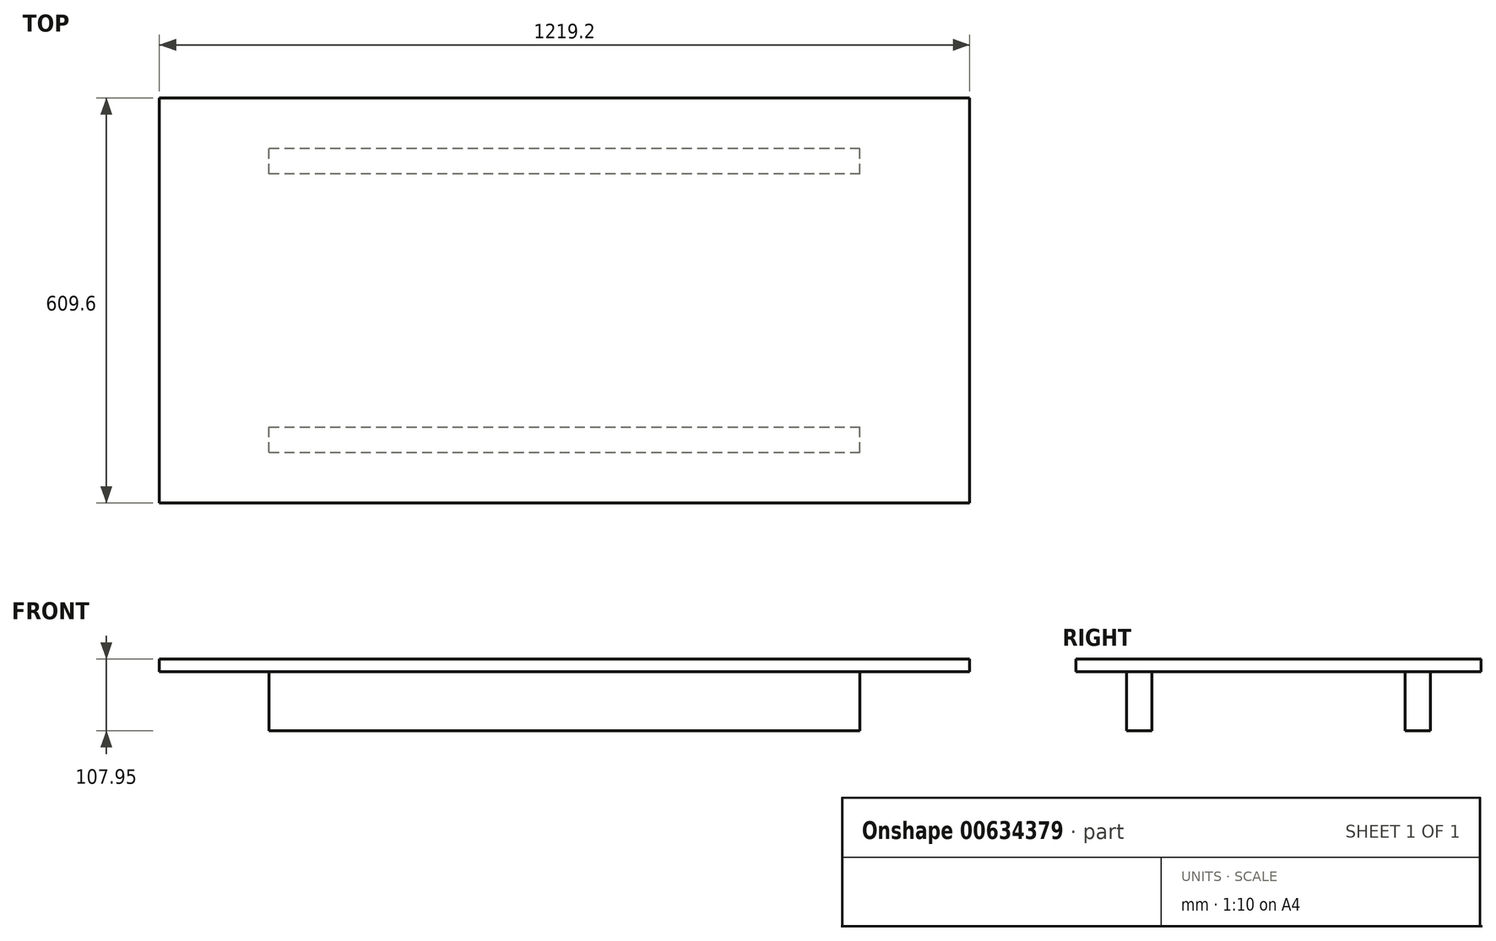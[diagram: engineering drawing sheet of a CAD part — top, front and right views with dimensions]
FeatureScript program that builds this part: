
annotation { "Feature Type Name" : "Feature", "Feature Type Description" : "" }
export const myFeature = defineFeature(function(context is Context, id is Id, definition is map)
    precondition{}
    {
        {
            var Q0;
            Q0=qCreatedBy(makeId("Top.planeOp"),FACE);
            var sketch = newSketch(context, id + "F0", { "sketchPlane" : qUnion([Q0])});
            skLineSegment(sketch, "E0.bottom", {"start": v(-609.6, 304.8) * mm, "end": v(609.6, 304.8) * mm});
            skLineSegment(sketch, "E0.top", {"start": v(-609.6, -304.8) * mm, "end": v(609.6, -304.8) * mm});
            skLineSegment(sketch, "E0.left", {"start": v(-609.6, 304.8) * mm, "end": v(-609.6, -304.8) * mm});
            skLineSegment(sketch, "E0.right", {"start": v(609.6, 304.8) * mm, "end": v(609.6, -304.8) * mm});
            skSolve(sketch);
        }
        {
            var Q0;
            Q0 = qSketchRegion(id + "F0", true);
            extrude(context, id + "F1", {"entities" : qUnion([Q0]), "depth" : 19.05 * mm, "offsetDistance" : 25.4 * mm});
        }
        {
            var Q0;
            Q0=makeQuery(id+"F1.opExtrude","CAP_FACE",FACE,{"disambiguationData":[OSD([sQuery(id+"F0.wireOp",EDGE,"E0.bottom"),sQuery(id+"F0.wireOp",EDGE,"E0.top"),sQuery(id+"F0.wireOp",EDGE,"E0.left"),sQuery(id+"F0.wireOp",EDGE,"E0.right")])],"isStart":true});
            var sketch = newSketch(context, id + "F2", { "sketchPlane" : qUnion([Q0])});
            skLineSegment(sketch, "E1.bottom", {"start": v(444.5, 228.6) * mm, "end": v(533.4, 228.6) * mm});
            skLineSegment(sketch, "E1.top", {"start": v(444.5, 190.5) * mm, "end": v(533.4, 190.5) * mm});
            skLineSegment(sketch, "E1.left", {"start": v(444.5, 228.6) * mm, "end": v(444.5, 190.5) * mm});
            skLineSegment(sketch, "E1.right", {"start": v(533.4, 228.6) * mm, "end": v(533.4, 190.5) * mm});
            skLineSegment(sketch, "E2.bottom", {"start": v(-533.4, 228.6) * mm, "end": v(-444.5, 228.6) * mm});
            skLineSegment(sketch, "E2.top", {"start": v(-533.4, 190.5) * mm, "end": v(-444.5, 190.5) * mm});
            skLineSegment(sketch, "E2.left", {"start": v(-533.4, 228.6) * mm, "end": v(-533.4, 190.5) * mm});
            skLineSegment(sketch, "E2.right", {"start": v(-444.5, 228.6) * mm, "end": v(-444.5, 190.5) * mm});
            skLineSegment(sketch, "E3.bottom", {"start": v(-533.4, -190.5) * mm, "end": v(-444.5, -190.5) * mm});
            skLineSegment(sketch, "E3.top", {"start": v(-533.4, -228.6) * mm, "end": v(-444.5, -228.6) * mm});
            skLineSegment(sketch, "E3.left", {"start": v(-533.4, -190.5) * mm, "end": v(-533.4, -228.6) * mm});
            skLineSegment(sketch, "E3.right", {"start": v(-444.5, -190.5) * mm, "end": v(-444.5, -228.6) * mm});
            skLineSegment(sketch, "E4.bottom", {"start": v(444.5, -190.5) * mm, "end": v(533.4, -190.5) * mm});
            skLineSegment(sketch, "E4.top", {"start": v(444.5, -228.6) * mm, "end": v(533.4, -228.6) * mm});
            skLineSegment(sketch, "E4.left", {"start": v(444.5, -190.5) * mm, "end": v(444.5, -228.6) * mm});
            skLineSegment(sketch, "E4.right", {"start": v(533.4, -190.5) * mm, "end": v(533.4, -228.6) * mm});
            skLineSegment(sketch, "E5.bottom", {"start": v(-444.5, 228.6) * mm, "end": v(444.5, 228.6) * mm});
            skLineSegment(sketch, "E5.top", {"start": v(-444.5, 190.5) * mm, "end": v(444.5, 190.5) * mm});
            skLineSegment(sketch, "E6.bottom", {"start": v(533.4, 190.5) * mm, "end": v(488.95, 190.5) * mm});
            skLineSegment(sketch, "E6.top", {"start": v(533.4, -190.5) * mm, "end": v(488.95, -190.5) * mm});
            skLineSegment(sketch, "E7.bottom", {"start": v(444.5, -228.6) * mm, "end": v(-444.5, -228.6) * mm});
            skLineSegment(sketch, "E7.top", {"start": v(444.5, -190.5) * mm, "end": v(-444.5, -190.5) * mm});
            skLineSegment(sketch, "E7.left", {"start": v(444.5, -228.6) * mm, "end": v(444.5, -190.5) * mm});
            skLineSegment(sketch, "E7.right", {"start": v(-444.5, -228.6) * mm, "end": v(-444.5, -190.5) * mm});
            skLineSegment(sketch, "E8.bottom", {"start": v(-533.4, 190.5) * mm, "end": v(-495.3, 190.5) * mm});
            skLineSegment(sketch, "E8.top", {"start": v(-533.4, -190.5) * mm, "end": v(-495.3, -190.5) * mm});
            skLineSegment(sketch, "E8.left", {"start": v(-533.4, 190.5) * mm, "end": v(-533.4, -190.5) * mm});
            skLineSegment(sketch, "E8.right", {"start": v(-495.3, 190.5) * mm, "end": v(-495.3, -190.5) * mm});
            skLineSegment(sketch, "E9.bottom", {"start": v(533.4, 190.5) * mm, "end": v(495.3, 190.5) * mm});
            skLineSegment(sketch, "E9.top", {"start": v(533.4, -190.5) * mm, "end": v(495.3, -190.5) * mm});
            skLineSegment(sketch, "E9.left", {"start": v(533.4, 190.5) * mm, "end": v(533.4, -190.5) * mm});
            skLineSegment(sketch, "E9.right", {"start": v(495.3, 190.5) * mm, "end": v(495.3, -190.5) * mm});
            skSolve(sketch);
        }
        {
            var Q0;
            Q0=makeQuery(id+"F2.imprint","IMPRINT",FACE,{"disambiguationData":[TD([[makeQuery(id+"F2.imprint","IMPRINT",EDGE,{"derivedFrom":sQuery(id+"F2.wireOp",EDGE,"E5.bottom")}),-1.0]])]});
            var Q1;
            Q1=makeQuery(id+"F2.imprint","IMPRINT",FACE,{"disambiguationData":[TD([[makeQuery(id+"F2.imprint","IMPRINT",EDGE,{"derivedFrom":sQuery(id+"F2.wireOp",EDGE,"E7.bottom")}),-1.0]])]});
            var Q2;
            Q2=makeQuery(id+"F2.imprint","IMPRINT",FACE,{"disambiguationData":[TD([[makeQuery(id+"F2.imprint","IMPRINT",EDGE,{"derivedFrom":sQuery(id+"F2.wireOp",EDGE,"E8.bottom")}),-1.0]])]});
            var Q3;
            Q3=makeQuery(id+"F2.imprint","IMPRINT",FACE,{"disambiguationData":[TD([[makeQuery(id+"F2.imprint","IMPRINT",EDGE,{"derivedFrom":sQuery(id+"F2.wireOp",EDGE,"E9.bottom")}),1.0]])]});
            extrude(context, id + "F3", {"entities" : qUnion([Q0, Q1, Q2, Q3]), "operationType" : NewBodyOperationType.ADD, "depth" : 88.9 * mm, "offsetDistance" : 25.4 * mm});
        }
    });
